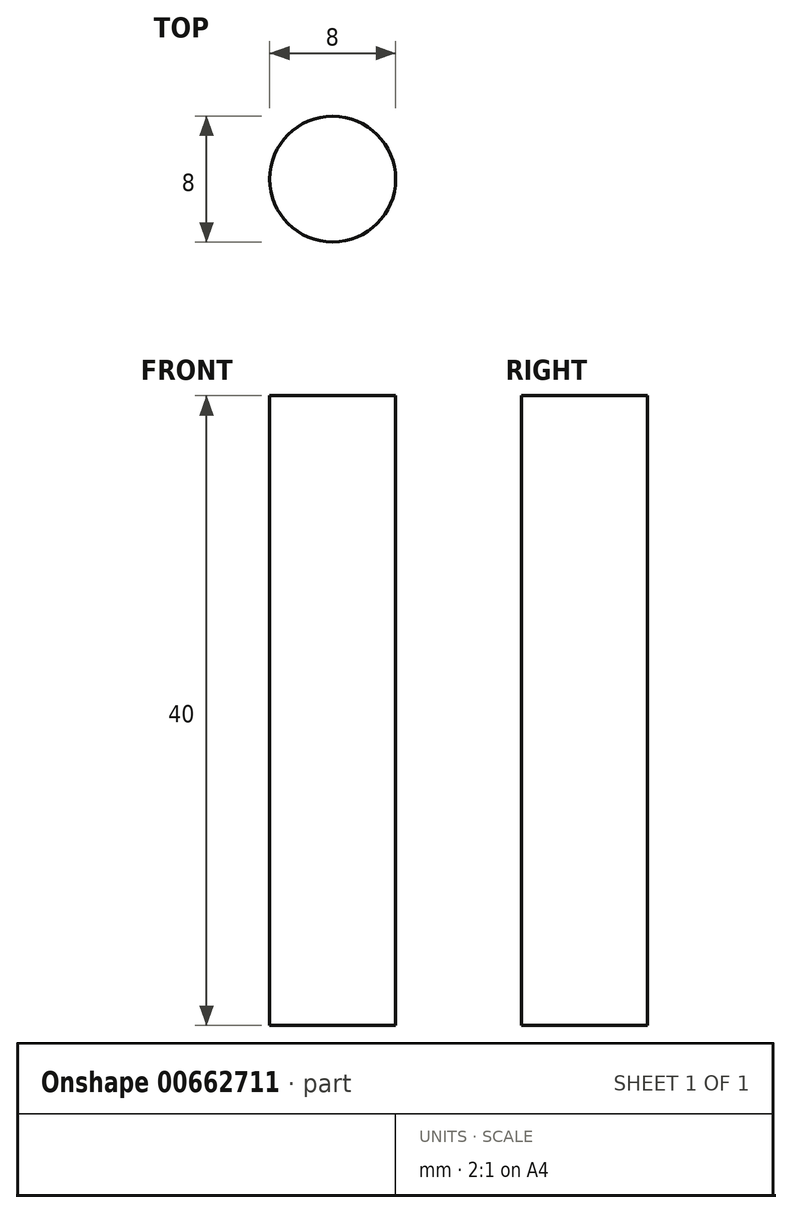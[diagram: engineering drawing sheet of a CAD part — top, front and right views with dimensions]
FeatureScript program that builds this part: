
annotation { "Feature Type Name" : "Feature", "Feature Type Description" : "" }
export const myFeature = defineFeature(function(context is Context, id is Id, definition is map)
    precondition{}
    {
        {
            var Q0;
            Q0=qCreatedBy(makeId("Top.planeOp"),FACE);
            var sketch = newSketch(context, id + "F0", { "sketchPlane" : qUnion([Q0])});
            skCircle(sketch, "E0", {"center": v(0, 0) * mm, "radius": 4 * mm});
            skSolve(sketch);
        }
        {
            var Q0;
            Q0=makeQuery(id+"F0.imprint","IMPRINT",FACE,{"disambiguationData":[TD([[makeQuery(id+"F0.imprint","IMPRINT",EDGE,{"derivedFrom":sQuery(id+"F0.wireOp",EDGE,"E0")}),1.0]])]});
            extrude(context, id + "F1", {"entities" : qUnion([Q0]), "depth" : 40 * mm, "offsetDistance" : 25 * mm});
        }
    });
